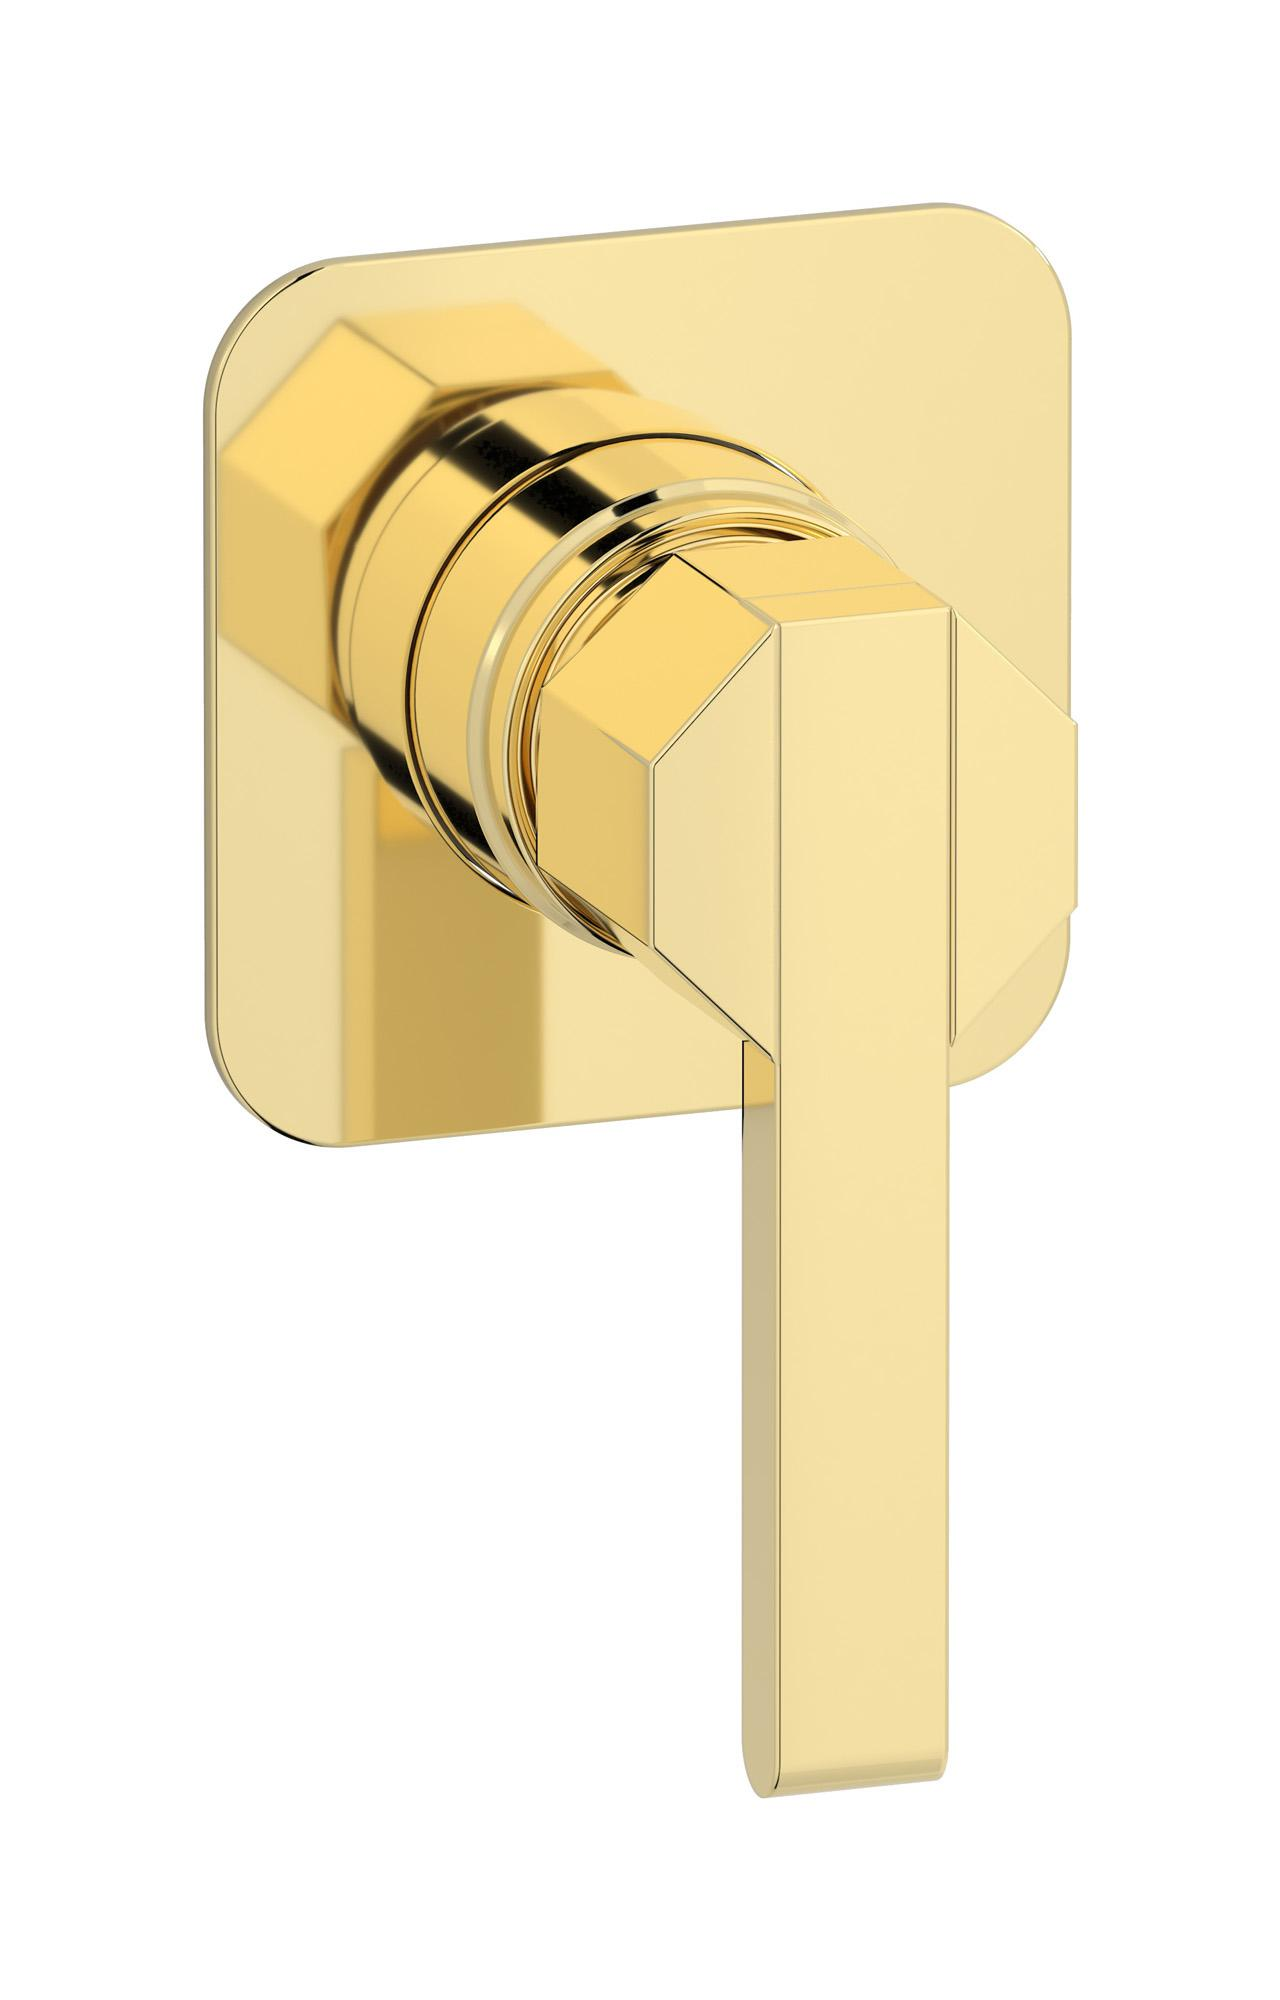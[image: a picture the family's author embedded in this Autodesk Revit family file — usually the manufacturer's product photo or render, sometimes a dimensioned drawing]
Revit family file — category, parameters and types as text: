
# Revit family: BL300
name_source: partatom
category: Apparecchi idraulici
units: mm (PartAtom-declared; Revit-internal decimal feet)

## family parameters
Basato su piano di lavoro = No
Condiviso = No
Mantieni orientamento annotazione = No
Numero OmniClass = 23.45.55.17
Punto di calcolo locali = No
Quota connettore circolare = Usa diametro
Sempre verticale = Sì
Taglio con vuoti quando caricato = No
Tipo di parte = Normale
Titolo OmniClass = Mixing Faucets

## types (7) — shared parameters
Cold water inlet = 10 mm  [stored 0.0328084 ft]
Commenti sul tipo = Wall mixer
Connessione CW = No
Connessione HW = No
Connessione di scarico = No
Connessione di ventilazione = No
Descrizione = Exposed parts for manual wall mixer
Hot water flow = 0,0 L/s
Hot water inlet = 10 mm  [stored 0.0328084 ft]
Produttore = IB Rubinetterie S.p.A.
zero-valued in all types: Prospetto di default

## per-type parameters (varying)
| type | Finishes surface | Immagine tipo | Modello | URL |
| Chrome | IB_Chrome | BL300CC.jpg | BL300CC | weareib.it/products/bathroom/belmondo-belmondo-elle/ebl300cc/ |
| Platinum | IB_Platinum | BL300PL.jpg | BL300PL | weareib.it/products/bathroom/belmondo-belmondo-elle/ebl300pl/ |
| Pale gold | IB_Pale gold | BL300II.jpg | BL300II | weareib.it/products/bathroom/belmondo-belmondo-elle/ebl300ii/ |
| Gold | IB_gold | BL300OO.jpg | BL300OO | weareib.it/products/bathroom/belmondo-belmondo-elle/ebl300oo/ |
| Rose gold | IB_Rose gold | BL300RS.jpg | BL300RS | weareib.it/products/bathroom/belmondo-belmondo-elle/ebl300rs/ |
| Modern Bronze | IB_Modern bronze | BL300MB.jpg | BL300MB | https://www.weareib.it |
| Brushed Nickel | IB_Brushed nickel | BL300SS.jpg | BL300SS | https://www.weareib.it |

note: [stored X ft] marks values corroborated as IEEE doubles in the binary element streams (Revit-internal decimal feet)
